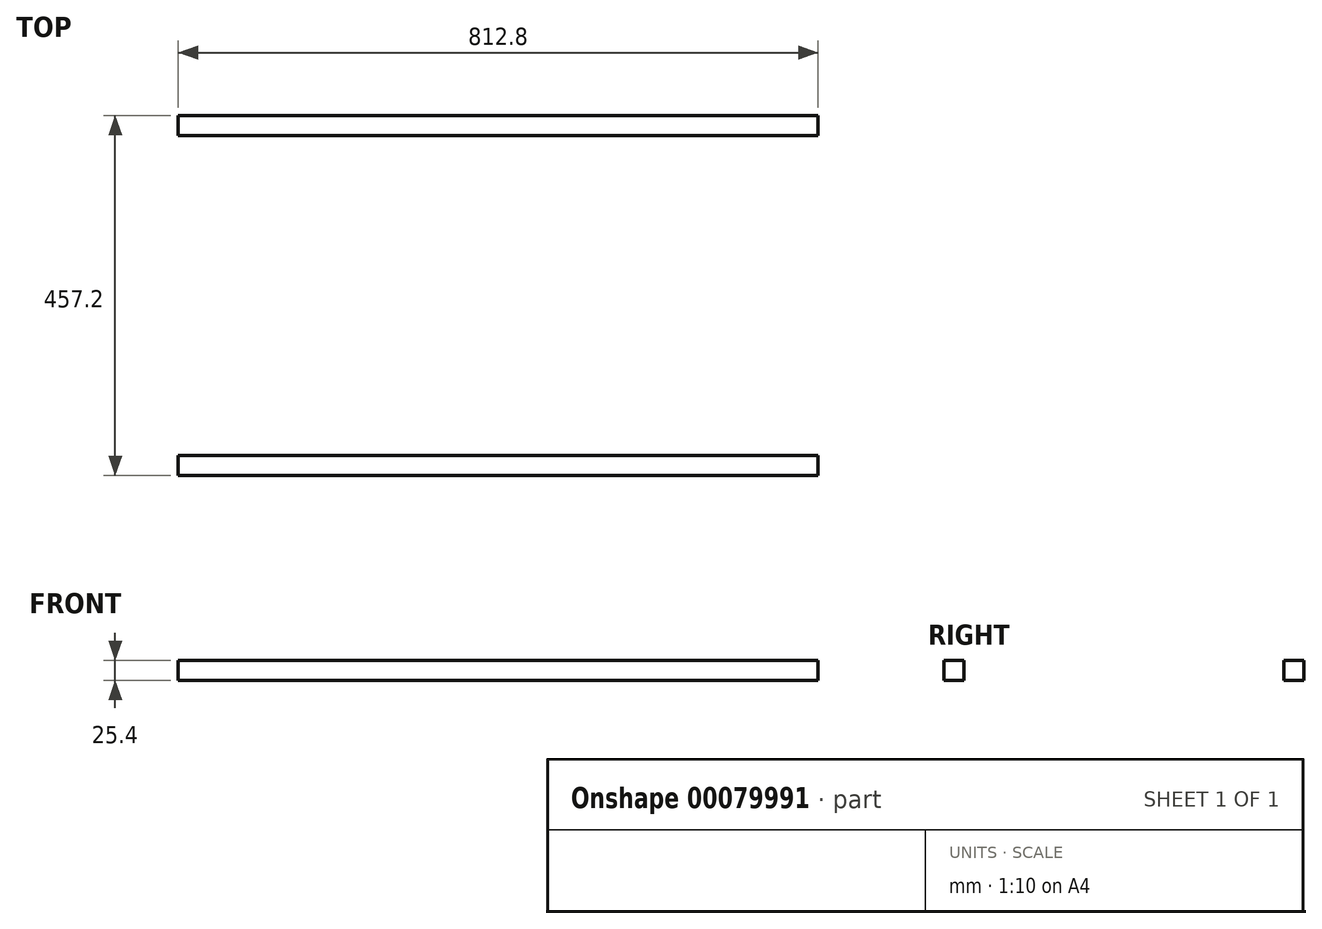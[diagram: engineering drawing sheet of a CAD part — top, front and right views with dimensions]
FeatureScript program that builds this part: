
annotation { "Feature Type Name" : "Feature", "Feature Type Description" : "" }
export const myFeature = defineFeature(function(context is Context, id is Id, definition is map)
    precondition{}
    {
        {
            var Q0;
            Q0=qCreatedBy(makeId("Top.planeOp"),FACE);
            var sketch = newSketch(context, id + "F0", { "sketchPlane" : qUnion([Q0])});
            skLineSegment(sketch, "E0.bottom", {"start": v(406.4, 12.7) * mm, "end": v(-406.4, 12.7) * mm});
            skLineSegment(sketch, "E0.top", {"start": v(406.4, -12.7) * mm, "end": v(-406.4, -12.7) * mm});
            skLineSegment(sketch, "E0.left", {"start": v(406.4, 12.7) * mm, "end": v(406.4, -12.7) * mm});
            skLineSegment(sketch, "E0.right", {"start": v(-406.4, 12.7) * mm, "end": v(-406.4, -12.7) * mm});
            skPoint(sketch, "E0.middle", {"position": v(0, 0) * mm});
            skLineSegment(sketch, "E1.bottom", {"start": v(406.4, 12.7) * mm, "end": v(381, 12.7) * mm});
            skLineSegment(sketch, "E1.top", {"start": v(406.4, 419.1) * mm, "end": v(381, 419.1) * mm});
            skLineSegment(sketch, "E1.left", {"start": v(406.4, 12.7) * mm, "end": v(406.4, 419.1) * mm});
            skLineSegment(sketch, "E1.right", {"start": v(381, 12.7) * mm, "end": v(381, 419.1) * mm});
            skLineSegment(sketch, "E2.bottom", {"start": v(-406.4, 12.7) * mm, "end": v(-381, 12.7) * mm});
            skLineSegment(sketch, "E2.top", {"start": v(-406.4, 419.1) * mm, "end": v(-381, 419.1) * mm});
            skLineSegment(sketch, "E2.left", {"start": v(-406.4, 12.7) * mm, "end": v(-406.4, 419.1) * mm});
            skLineSegment(sketch, "E2.right", {"start": v(-381, 12.7) * mm, "end": v(-381, 419.1) * mm});
            skLineSegment(sketch, "E3.bottom", {"start": v(-381, 419.1) * mm, "end": v(355.6, 419.1) * mm});
            skLineSegment(sketch, "E4.bottom", {"start": v(406.4, 419.1) * mm, "end": v(-406.4, 419.1) * mm});
            skLineSegment(sketch, "E4.top", {"start": v(406.4, 444.5) * mm, "end": v(-406.4, 444.5) * mm});
            skLineSegment(sketch, "E4.left", {"start": v(406.4, 419.1) * mm, "end": v(406.4, 444.5) * mm});
            skLineSegment(sketch, "E4.right", {"start": v(-406.4, 419.1) * mm, "end": v(-406.4, 444.5) * mm});
            skLineSegment(sketch, "E5.bottom", {"start": v(-177.8, 419.1) * mm, "end": v(-152.4, 419.1) * mm});
            skLineSegment(sketch, "E5.top", {"start": v(-177.8, 12.7) * mm, "end": v(-152.4, 12.7) * mm});
            skLineSegment(sketch, "E5.left", {"start": v(-177.8, 419.1) * mm, "end": v(-177.8, 12.7) * mm});
            skLineSegment(sketch, "E5.right", {"start": v(-152.4, 419.1) * mm, "end": v(-152.4, 12.7) * mm});
            skLineSegment(sketch, "E6", {"start": v(-381, 419.1) * mm, "end": v(-177.8, 419.1) * mm});
            skLineSegment(sketch, "E7", {"start": v(-152.4, 419.1) * mm, "end": v(381, 419.1) * mm});
            skLineSegment(sketch, "E8", {"start": v(-177.8, 160.69) * mm, "end": v(406.4, 160.69) * mm, "construction": true});
            skSolve(sketch);
        }
        {
            var Q0;
            Q0=makeQuery(id+"F0.imprint","IMPRINT",FACE,{"disambiguationData":[TD([[makeQuery(id+"F0.imprint","IMPRINT",EDGE,{"derivedFrom":sQuery(id+"F0.wireOp",EDGE,"E2.bottom")}),1.0]])]});
            var Q1;
            Q1=makeQuery(id+"F0.imprint","IMPRINT",FACE,{"disambiguationData":[TD([[makeQuery(id+"F0.imprint","IMPRINT",EDGE,{"derivedFrom":sQuery(id+"F0.wireOp",EDGE,"E4.top")}),1.0]])]});
            var Q2;
            Q2=makeQuery(id+"F0.imprint","IMPRINT",FACE,{"disambiguationData":[TD([[makeQuery(id+"F0.imprint","IMPRINT",EDGE,{"derivedFrom":sQuery(id+"F0.wireOp",EDGE,"E5.bottom")}),-1.0]])]});
            var Q3;
            Q3=makeQuery(id+"F0.imprint","IMPRINT",FACE,{"disambiguationData":[TD([[makeQuery(id+"F0.imprint","IMPRINT",EDGE,{"derivedFrom":sQuery(id+"F0.wireOp",EDGE,"E1.bottom")}),-1.0]])]});
            var Q4;
            Q4=makeQuery(id+"F0.imprint","IMPRINT",FACE,{"disambiguationData":[TD([[makeQuery(id+"F0.imprint","IMPRINT",EDGE,{"derivedFrom":sQuery(id+"F0.wireOp",EDGE,"E0.top")}),-1.0]])]});
            extrude(context, id + "F1", {"entities" : qUnion([Q0, Q1, Q2, Q3, Q4]), "endBound" : BoundingType.SYMMETRIC, "depth" : 25.4 * mm});
        }
    });
